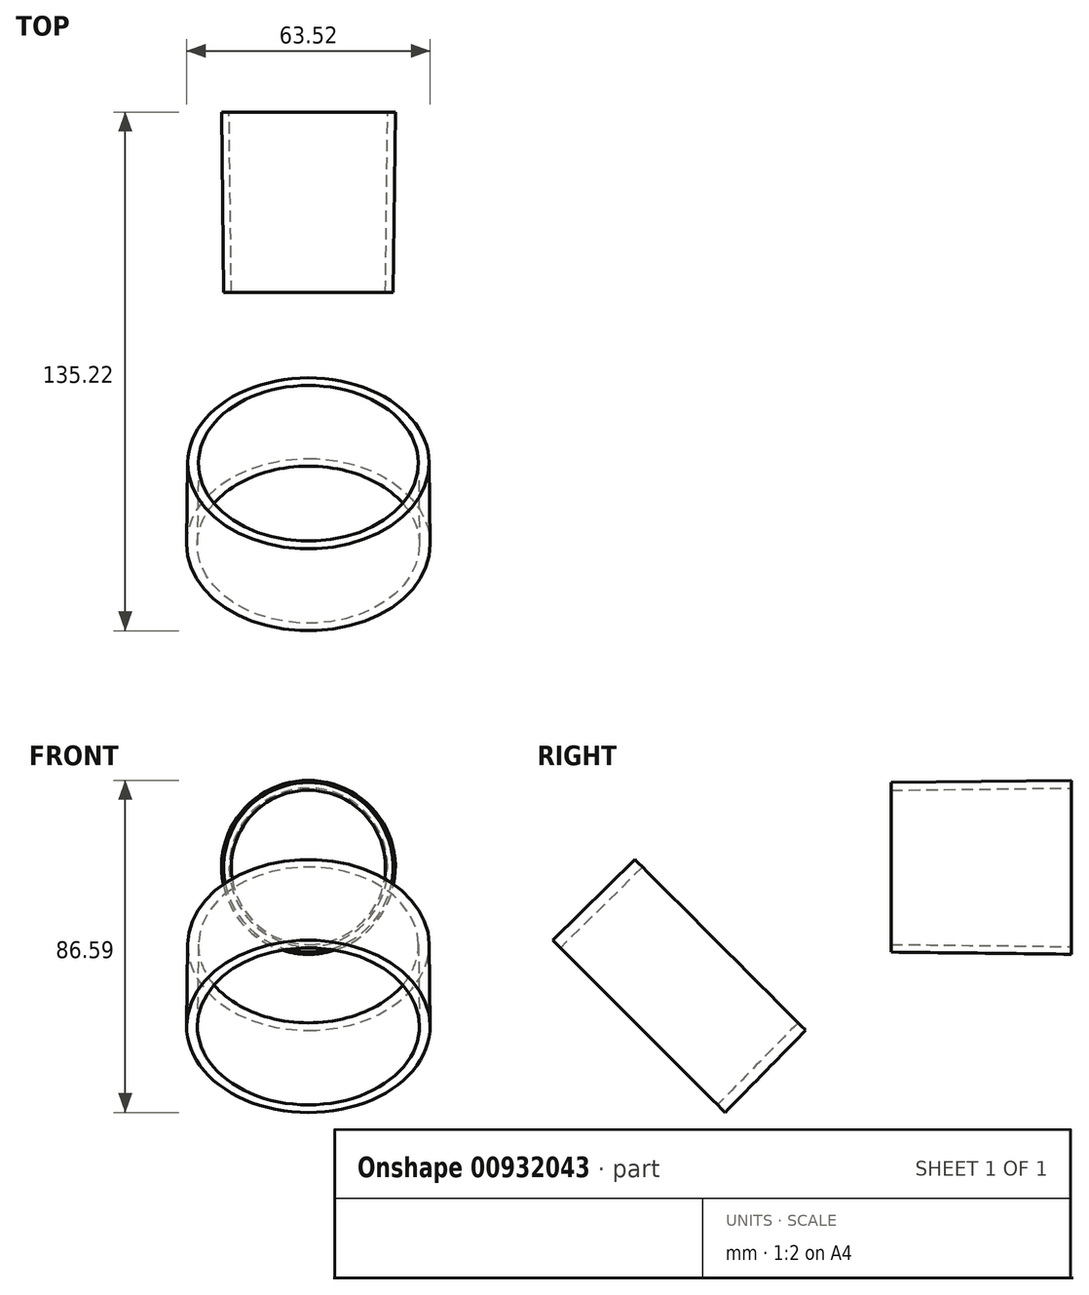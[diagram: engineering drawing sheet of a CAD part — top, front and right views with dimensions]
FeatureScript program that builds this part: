
annotation { "Feature Type Name" : "Feature", "Feature Type Description" : "" }
export const myFeature = defineFeature(function(context is Context, id is Id, definition is map)
    precondition{}
    {
        {
            var Q0;
            Q0=qCreatedBy(makeId("Front.planeOp"),FACE);
            var sketch = newSketch(context, id + "F0", { "sketchPlane" : qUnion([Q0])});
            skCircle(sketch, "E0", {"center": v(0, 0) * mm, "radius": 22.1 * mm});
            skCircle(sketch, "E1.0", {"center": v(0, 0) * mm, "radius": 20.1 * mm, "construction": true});
            skSolve(sketch);
        }
        {
            var Q0;
            Q0 = qSketchRegion(id + "F0", true);
            extrude(context, id + "F1", {"entities" : qUnion([Q0]), "oppositeDirection" : true, "depth" : 47 * mm, "offsetDistance" : 25 * mm, "hasDraft" : true, "draftAngle" : 0.7 * degree});
        }
        {
            var Q0;
            Q0=makeQuery(id+"F1.opExtrude","CAP_FACE",FACE,{"disambiguationData":[OSD([sQuery(id+"F0.wireOp",EDGE,"E0")])],"isStart":false});
            var Q1;
            Q1=makeQuery(id+"F1.opExtrude","CAP_FACE",FACE,{"disambiguationData":[OSD([sQuery(id+"F0.wireOp",EDGE,"E0")])],"isStart":true});
            shell(context, id + "F2", {"entities" : qUnion([Q0, Q1]), "thickness" : 2 * mm});
        }
        {
            var Q0;
            Q0=qCreatedBy(makeId("Front.planeOp"),FACE);
            var sketch = newSketch(context, id + "F3", { "sketchPlane" : qUnion([Q0])});
            skCircle(sketch, "E2", {"center": v(0, 0) * mm, "radius": 31.5 * mm});
            skLineSegment(sketch, "E3", {"start": v(-31.5, 0) * mm, "end": v(31.5, 0) * mm, "construction": true});
            skSolve(sketch);
        }
        {
            var Q0;
            Q0=makeQuery(id+"F3.imprint","IMPRINT",FACE,{"disambiguationData":[TD([[makeQuery(id+"F3.imprint","IMPRINT",EDGE,{"derivedFrom":sQuery(id+"F3.wireOp",EDGE,"E2")}),1.0]])]});
            extrude(context, id + "F4", {"entities" : qUnion([Q0]), "depth" : 30 * mm, "offsetDistance" : 25 * mm, "hasDraft" : true, "draftAngle" : .5 * degree});
        }
        {
            var Q0;
            Q0=makeQuery(id+"F4.opExtrude","CAP_FACE",FACE,{"disambiguationData":[OSD([sQuery(id+"F3.wireOp",EDGE,"E2")])],"isStart":false});
            var Q1;
            {var subQ1=sQuery(id+"F3.wireOp",EDGE,"E2");Q1=makeQuery(id+"F4.boolean.opBoolean","SPLIT",FACE,{"disambiguationData":[TD([makeQuery(id+"F4.opExtrude","SWEPT_FACE",FACE,{"disambiguationData":[OSD([subQ1])]})])],"derivedFrom":makeQuery(id+"F4.opExtrude","CAP_FACE",FACE,{"disambiguationData":[OSD([subQ1])],"isStart":true})});}
            shell(context, id + "F5", {"entities" : qUnion([Q0, Q1]), "thickness" : 2.8 * mm});
        }
        {
            var Q0;
            Q0=qCreatedBy(makeId("Right.planeOp"),FACE);
            var sketch = newSketch(context, id + "F6", { "sketchPlane" : qUnion([Q0])});
            skLineSegment(sketch, "E4", {"start": v(0, 0) * mm, "end": v(-44.55, -20.25) * mm, "construction": true});
            skSolve(sketch);
        }
        {
            var Q0;
            Q0=makeQuery(id+"F4.opExtrude","SWEPT_BODY",BODY,{"disambiguationData":[OSD([sQuery(id+"F3.wireOp",EDGE,"E2")])]});
            var Q1;
            Q1=sQuery(id+"F3.wireOp",EDGE,"E3");
            transform(context, id + "F7", {"entities" : qUnion([Q0]), "transformType" : TransformType.ROTATION, "transformAxis" : qUnion([Q1]), "angle" : 45 * degree, "makeCopy" : false});
        }
        {
            var Q0;
            Q0=makeQuery(id+"F4.opExtrude","SWEPT_BODY",BODY,{"disambiguationData":[OSD([sQuery(id+"F3.wireOp",EDGE,"E2")])]});
            var Q1;
            Q1=sQuery(id+"F6.wireOp",EDGE,"E4");
            transform(context, id + "F8", {"entities" : qUnion([Q0]), "transformType" : TransformType.TRANSLATION_ENTITY, "oppositeDirectionEntity" : false, "transformLine" : qUnion([Q1]), "makeCopy" : false});
        }
        {
            var Q0;
            Q0=qCreatedBy(makeId("Right.planeOp"),FACE);
            var sketch = newSketch(context, id + "F9", { "sketchPlane" : qUnion([Q0])});
            skLineSegment(sketch, "E5", {"start": v(-22.28, -42.52) * mm, "end": v(-43.3, -63.92) * mm});
            skLineSegment(sketch, "E6", {"start": v(-88.22, -19) * mm, "end": v(-66.83, 2.03) * mm});
            skLineSegment(sketch, "E7", {"start": v(47, 22.67) * mm, "end": v(0, 22.1) * mm});
            skLineSegment(sketch, "E8", {"start": v(0, -22.1) * mm, "end": v(47, -22.67) * mm});
            skFitSpline(sketch, "E9", {"points": [v(-66.83, 2.03) * mm, v(-34.1, 17.6) * mm, v(0, 22.1) * mm], "startDerivative": vector(61.8, 60.74) * mm, "endDerivative": vector(101.36, 1.24) * mm});
            skFitSpline(sketch, "E10", {"points": [v(-22.28, -42.52) * mm, v(-11.32, -29.49) * mm, v(0, -22.1) * mm], "startDerivative": vector(24.1, 24.52) * mm, "endDerivative": vector(30.66, -0.37) * mm});
            skLineSegment(sketch, "E11.0", {"start": v(47, -22.67) * mm, "end": v(47, 22.67) * mm});
            skLineSegment(sketch, "E12.0", {"start": v(-43.3, -63.92) * mm, "end": v(-88.22, -19) * mm});
            skLineSegment(sketch, "E13.0", {"start": v(-22.28, -42.52) * mm, "end": v(-66.83, 2.03) * mm});
            skLineSegment(sketch, "E14.0", {"start": v(0, -22.1) * mm, "end": v(0, 22.1) * mm});
            skLineSegment(sketch, "E15", {"start": v(-65.77, -41.46) * mm, "end": v(-44.55, -20.25) * mm});
            skLineSegment(sketch, "E16", {"start": v(0, 0) * mm, "end": v(47, 0) * mm});
            skFitSpline(sketch, "E17", {"points": [v(-44.55, -20.25) * mm, v(0, 0) * mm], "startDerivative": vector(34.6, 34.6) * mm, "endDerivative": vector(48.94, 0) * mm});
            skSolve(sketch);
        }
        {
            var Q0;
            Q0=sQuery(id+"F9.wireOp",EDGE,"E15");
            var Q1;
            Q1=sQuery(id+"F9.wireOp",EDGE,"E17");
            var Q2;
            Q2=sQuery(id+"F9.wireOp",EDGE,"E16");
            var Q3;
            Q3=makeQuery(id+"F4.opExtrude","CAP_EDGE",EDGE,{"disambiguationData":[OSD([sQuery(id+"F3.wireOp",EDGE,"E2")])],"isStart":false});
            var Q4;
            Q4=makeQuery(id+"F4.opExtrude","CAP_EDGE",EDGE,{"disambiguationData":[OSD([sQuery(id+"F3.wireOp",EDGE,"E2")])],"isStart":true});
            var Q5;
            Q5=makeQuery(id+"F1.opExtrude","CAP_EDGE",EDGE,{"disambiguationData":[OSD([sQuery(id+"F0.wireOp",EDGE,"E0")])],"isStart":true});
            var Q6;
            Q6=makeQuery(id+"F1.opExtrude","CAP_EDGE",EDGE,{"disambiguationData":[OSD([sQuery(id+"F0.wireOp",EDGE,"E0")])],"isStart":false});
            loft(context, id + "F10", {"bodyType" : ToolBodyType.SURFACE, "addSections" : true, "spine" : qUnion([Q0, Q1, Q2]), "sectionCount" : 10, "wireProfilesArray" : [{ "wireProfileEntities" : qUnion([Q3]) }, { "wireProfileEntities" : qUnion([Q4]) }, { "wireProfileEntities" : qUnion([Q5]) }, { "wireProfileEntities" : qUnion([Q6]) }]});
        }
    });
